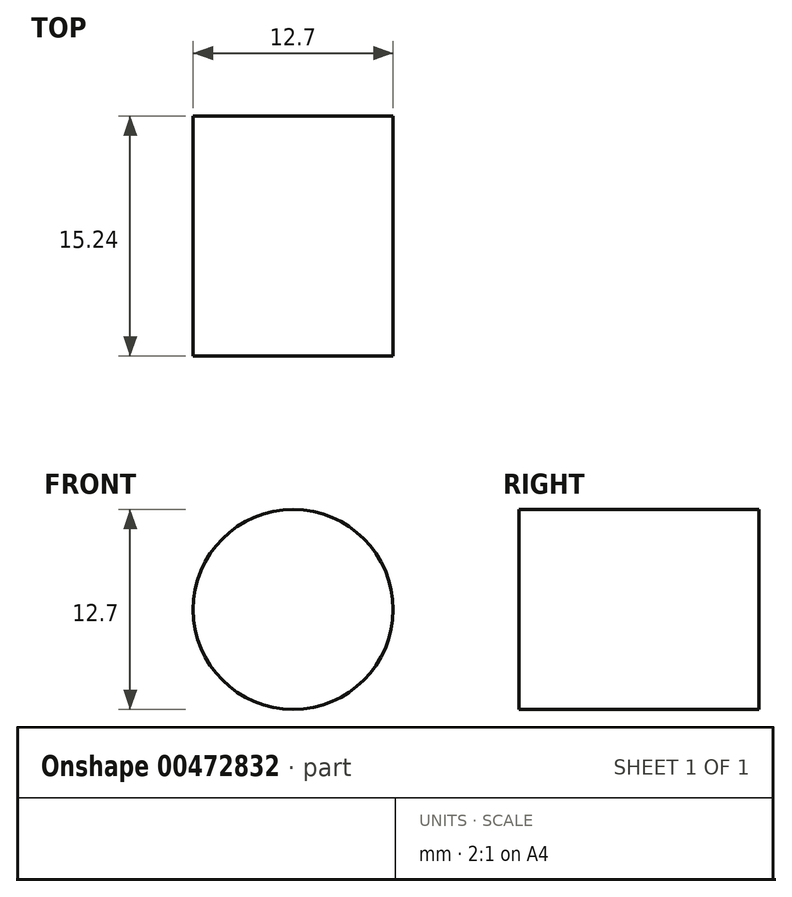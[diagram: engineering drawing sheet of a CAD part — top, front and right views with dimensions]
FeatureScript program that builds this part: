
annotation { "Feature Type Name" : "Feature", "Feature Type Description" : "" }
export const myFeature = defineFeature(function(context is Context, id is Id, definition is map)
    precondition{}
    {
        {
            var Q0;
            Q0=qCreatedBy(makeId("Front.planeOp"),FACE);
            var sketch = newSketch(context, id + "F0", { "sketchPlane" : qUnion([Q0])});
            skCircle(sketch, "E0", {"center": v(0, 0) * mm, "radius": 6.35 * mm});
            skSolve(sketch);
        }
        {
            var Q0;
            Q0=makeQuery(id+"F0.imprint","IMPRINT",FACE,{"disambiguationData":[TD([[makeQuery(id+"F0.imprint","IMPRINT",EDGE,{"derivedFrom":sQuery(id+"F0.wireOp",EDGE,"E0")}),1.0]])]});
            extrude(context, id + "F1", {"entities" : qUnion([Q0]), "depth" : 15.24 * mm});
        }
    });
